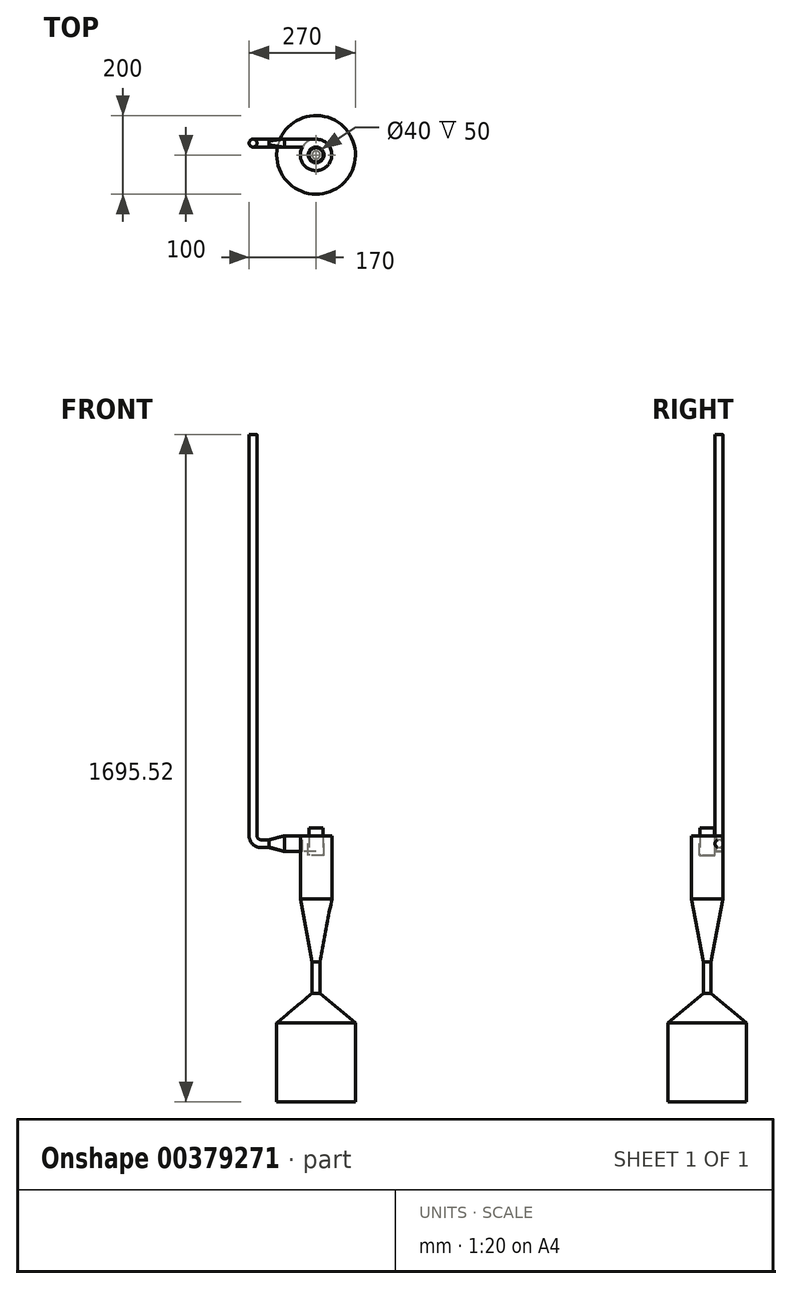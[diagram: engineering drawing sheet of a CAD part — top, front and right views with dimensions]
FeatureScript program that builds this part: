
annotation { "Feature Type Name" : "Feature", "Feature Type Description" : "" }
export const myFeature = defineFeature(function(context is Context, id is Id, definition is map)
    precondition{}
    {
        {
            var Q0;
            Q0=qCreatedBy(makeId("Top.planeOp"),FACE);
            var sketch = newSketch(context, id + "F0", { "sketchPlane" : qUnion([Q0])});
            skCircle(sketch, "E0", {"center": v(0, 0) * mm, "radius": 40 * mm});
            skSolve(sketch);
        }
        {
            var Q0;
            Q0=qSketchRegion(id+"F0",true);
            extrude(context, id + "F1", {"entities" : qUnion([Q0]), "oppositeDirection" : true, "depth" : 160 * mm});
        }
        {
            var Q0;
            Q0=makeQuery(id+"F1.opExtrude","CAP_FACE",FACE,{"disambiguationData":[OSD([sQuery(id+"F0.wireOp",EDGE,"E0")])],"isStart":false});
            cPlane(context, id + "F2", {"entities" : qUnion([Q0]), "cplaneType" : CPlaneType.OFFSET, "offset" : 160 * mm, "width" : 150 * mm, "height" : 150 * mm});
        }
        {
            var Q0;
            Q0=qCreatedBy(id+"F2.planeOp",FACE);
            var sketch = newSketch(context, id + "F3", { "sketchPlane" : qUnion([Q0])});
            skCircle(sketch, "E1", {"center": v(0, 0) * mm, "radius": 10 * mm});
            skSolve(sketch);
        }
        {
            var Q1;
            Q1=makeQuery(id+"F3.imprint","IMPRINT",FACE,{"disambiguationData":[TD([[makeQuery(id+"F3.imprint","IMPRINT",EDGE,{"derivedFrom":sQuery(id+"F3.wireOp",EDGE,"E1")}),1.0]])]});
            var Q2;
            Q2=makeQuery(id+"F1.opExtrude","CAP_FACE",FACE,{"disambiguationData":[OSD([sQuery(id+"F0.wireOp",EDGE,"E0")])],"isStart":false});
            loft(context, id + "F4", {"operationType" : NewBodyOperationType.ADD, "sheetProfilesArray" : [{ "sheetProfileEntities" : qUnion([Q1]) }, { "sheetProfileEntities" : qUnion([Q2]) }]});
        }
        {
            var Q0;
            Q0=makeQuery(id+"F4.opLoft","CAP_FACE",FACE,{"disambiguationData":[OSD([makeQuery(id+"F3.imprint","IMPRINT",FACE,{"disambiguationData":[TD([[makeQuery(id+"F3.imprint","IMPRINT",EDGE,{"derivedFrom":sQuery(id+"F3.wireOp",EDGE,"E1")}),1.0]])]})])],"isStart":true});
            extrude(context, id + "F5", {"entities" : qUnion([Q0]), "operationType" : NewBodyOperationType.ADD, "depth" : 40 * mm});
        }
        {
            var Q0;
            Q0=qCreatedBy(makeId("Top.planeOp"),FACE);
            var sketch = newSketch(context, id + "F6", { "sketchPlane" : qUnion([Q0])});
            skLineSegment(sketch, "E2.bottom", {"start": v(0, 20) * mm, "end": v(-80, 20) * mm});
            skLineSegment(sketch, "E2.top", {"start": v(0, 40) * mm, "end": v(-80, 40) * mm});
            skLineSegment(sketch, "E2.left", {"start": v(0, 20) * mm, "end": v(0, 40) * mm});
            skLineSegment(sketch, "E2.right", {"start": v(-80, 20) * mm, "end": v(-80, 40) * mm});
            skSolve(sketch);
        }
        {
            var Q0;
            Q0=makeQuery(id+"F6.imprint","IMPRINT",FACE,{"disambiguationData":[TD([[makeQuery(id+"F6.imprint","IMPRINT",EDGE,{"derivedFrom":sQuery(id+"F6.wireOp",EDGE,"E2.bottom")}),-1.0]])]});
            extrude(context, id + "F7", {"entities" : qUnion([Q0]), "operationType" : NewBodyOperationType.ADD, "oppositeDirection" : true, "depth" : 40 * mm});
        }
        {
            var Q0;
            Q0=makeQuery(id+"F7.boolean.opBoolean","MERGE",FACE,{"derivedFrom":[makeQuery(id+"F1.opExtrude","CAP_FACE",FACE,{"disambiguationData":[OSD([sQuery(id+"F0.wireOp",EDGE,"E0")])],"isStart":true}),makeQuery(id+"F7.opExtrude","CAP_FACE",FACE,{"disambiguationData":[OSD([sQuery(id+"F6.wireOp",EDGE,"E2.bottom"),sQuery(id+"F6.wireOp",EDGE,"E2.top"),sQuery(id+"F6.wireOp",EDGE,"E2.left"),sQuery(id+"F6.wireOp",EDGE,"E2.right")])],"isStart":true})]});
            var sketch = newSketch(context, id + "F8", { "sketchPlane" : qUnion([Q0])});
            skCircle(sketch, "E3", {"center": v(0, 0) * mm, "radius": 18 * mm});
            skSolve(sketch);
        }
        {
            var Q0;
            Q0=makeQuery(id+"F8.imprint","IMPRINT",FACE,{"disambiguationData":[TD([[makeQuery(id+"F8.imprint","IMPRINT",EDGE,{"derivedFrom":sQuery(id+"F8.wireOp",EDGE,"E3")}),1.0]])]});
            extrude(context, id + "F9", {"entities" : qUnion([Q0]), "operationType" : NewBodyOperationType.ADD, "depth" : 20 * mm});
        }
        {
            var Q0;
            Q0=makeQuery(id+"F7.boolean.opBoolean","MERGE",FACE,{"derivedFrom":[makeQuery(id+"F1.opExtrude","CAP_FACE",FACE,{"disambiguationData":[OSD([sQuery(id+"F0.wireOp",EDGE,"E0")])],"isStart":true}),makeQuery(id+"F7.opExtrude","CAP_FACE",FACE,{"disambiguationData":[OSD([sQuery(id+"F6.wireOp",EDGE,"E2.bottom"),sQuery(id+"F6.wireOp",EDGE,"E2.top"),sQuery(id+"F6.wireOp",EDGE,"E2.left"),sQuery(id+"F6.wireOp",EDGE,"E2.right")])],"isStart":true})]});
            var sketch = newSketch(context, id + "F10", { "sketchPlane" : qUnion([Q0])});
            skCircle(sketch, "E4", {"center": v(0, 0) * mm, "radius": 20 * mm});
            skSolve(sketch);
        }
        {
            var Q0;
            Q0=makeQuery(id+"F10.imprint","IMPRINT",FACE,{"disambiguationData":[TD([[makeQuery(id+"F10.imprint","IMPRINT",EDGE,{"derivedFrom":sQuery(id+"F10.wireOp",EDGE,"E4")}),1.0]])]});
            extrude(context, id + "F11", {"entities" : qUnion([Q0]), "operationType" : NewBodyOperationType.REMOVE, "oppositeDirection" : true, "depth" : 50 * mm});
        }
        {
            var Q0;
            Q0=makeQuery(id+"F7.opExtrude","SWEPT_FACE",FACE,{"disambiguationData":[OSD([sQuery(id+"F6.wireOp",EDGE,"E2.right")])]});
            cPlane(context, id + "F12", {"entities" : qUnion([Q0]), "cplaneType" : CPlaneType.OFFSET, "offset" : 40 * mm, "width" : 150 * mm, "height" : 150 * mm});
        }
        {
            var Q0;
            Q0=qCreatedBy(id+"F12.planeOp",FACE);
            var sketch = newSketch(context, id + "F13", { "sketchPlane" : qUnion([Q0])});
            skPoint(sketch, "E5.middle", {"position": v(-30, -20) * mm});
            skArc(sketch, "E6", {"start": v(-34.47, -11.06) * mm, "mid": v(-40, -20) * mm, "end": v(-34.47, -28.94) * mm});
            skArc(sketch, "E7", {"start": v(-25.53, -11.06) * mm, "mid": v(-30, -10) * mm, "end": v(-34.47, -11.06) * mm});
            skArc(sketch, "E8", {"start": v(-25.53, -28.94) * mm, "mid": v(-20, -20) * mm, "end": v(-25.53, -11.06) * mm});
            skArc(sketch, "E9", {"start": v(-34.47, -28.94) * mm, "mid": v(-30, -30) * mm, "end": v(-25.53, -28.94) * mm});
            skPoint(sketch, "E10.orphan", {"position": v(-20, 0) * mm});
            skPoint(sketch, "E5.top.start.orphan", {"position": v(-20, -40) * mm});
            skPoint(sketch, "E11.orphan", {"position": v(-40, 0) * mm});
            skPoint(sketch, "E12.end.orphan", {"position": v(-40, -40) * mm});
            skSolve(sketch);
        }
        {
            var Q1;
            Q1=makeQuery(id+"F13.imprint","IMPRINT",FACE,{"disambiguationData":[TD([[makeQuery(id+"F13.imprint","IMPRINT",EDGE,{"derivedFrom":sQuery(id+"F13.wireOp",EDGE,"E6")}),1.0]])]});
            var Q2;
            Q2=makeQuery(id+"F7.opExtrude","SWEPT_FACE",FACE,{"disambiguationData":[OSD([sQuery(id+"F6.wireOp",EDGE,"E2.right")])]});
            loft(context, id + "F14", {"operationType" : NewBodyOperationType.ADD, "sheetProfilesArray" : [{ "sheetProfileEntities" : qUnion([Q1]) }, { "sheetProfileEntities" : qUnion([Q2]) }]});
        }
        {
            var Q0;
            Q0=makeQuery(id+"F14.opLoft","CAP_FACE",FACE,{"disambiguationData":[OSD([makeQuery(id+"F13.imprint","IMPRINT",FACE,{"disambiguationData":[TD([[makeQuery(id+"F13.imprint","IMPRINT",EDGE,{"derivedFrom":sQuery(id+"F13.wireOp",EDGE,"E6")}),1.0]])]})])],"isStart":true});
            extrude(context, id + "F15", {"entities" : qUnion([Q0]), "operationType" : NewBodyOperationType.ADD, "depth" : 20 * mm});
        }
        {
            var Q0;
            Q0=qCreatedBy(makeId("Front.planeOp"),FACE);
            cPlane(context, id + "F16", {"entities" : qUnion([Q0]), "cplaneType" : CPlaneType.OFFSET, "offset" : 30 * mm, "oppositeDirection" : true, "width" : 150 * mm, "height" : 150 * mm});
        }
        {
            var Q0;
            Q0=qCreatedBy(id+"F16.planeOp",FACE);
            var sketch = newSketch(context, id + "F17", { "sketchPlane" : qUnion([Q0])});
            skLineSegment(sketch, "E13", {"start": v(0, 0) * mm, "end": v(-140, 0) * mm});
            skLineSegment(sketch, "E14", {"start": v(-140, 0) * mm, "end": v(-140, -20) * mm});
            skArc(sketch, "E15", {"start": v(-140, -20) * mm, "mid": v(-154.14, -14.14) * mm, "end": v(-160, 0) * mm});
            skSolve(sketch);
        }
        {
            var Q0;
            Q0=makeQuery(id+"F15.opExtrude","CAP_FACE",FACE,{"disambiguationData":[OSD([makeQuery(id+"F13.imprint","IMPRINT",FACE,{"disambiguationData":[TD([[makeQuery(id+"F13.imprint","IMPRINT",EDGE,{"derivedFrom":sQuery(id+"F13.wireOp",EDGE,"E6")}),1.0]])]})])],"isStart":false});
            var Q1;
            Q1=sQuery(id+"F17.wireOp",EDGE,"E15");
            sweep(context, id + "F18", {"operationType" : NewBodyOperationType.ADD, "profiles" : qUnion([Q0]), "path" : qUnion([Q1])});
        }
        {
            var Q0;
            Q0=makeQuery(id+"F18.opSweep","CAP_FACE",FACE,{"disambiguationData":[OSD([makeQuery(id+"F13.imprint","IMPRINT",FACE,{"disambiguationData":[TD([[makeQuery(id+"F13.imprint","IMPRINT",EDGE,{"derivedFrom":sQuery(id+"F13.wireOp",EDGE,"E6")}),1.0]])]}),sQuery(id+"F17.wireOp",VERTEX,"E15.end")])],"isStart":false});
            extrude(context, id + "F19", {"entities" : qUnion([Q0]), "operationType" : NewBodyOperationType.ADD, "depth" : 20 * mm});
        }
        {
            var Q0;
            Q0=makeQuery(id+"F19.opExtrude","CAP_FACE",FACE,{"disambiguationData":[OSD([makeQuery(id+"F13.imprint","IMPRINT",FACE,{"disambiguationData":[TD([[makeQuery(id+"F13.imprint","IMPRINT",EDGE,{"derivedFrom":sQuery(id+"F13.wireOp",EDGE,"E6")}),1.0]])]}),sQuery(id+"F17.wireOp",VERTEX,"E15.end")])],"isStart":false});
            extrude(context, id + "F20", {"entities" : qUnion([Q0]), "operationType" : NewBodyOperationType.ADD, "depth" : 1000 * mm});
        }
        {
            var Q0;
            Q0=makeQuery(id+"F5.opExtrude","CAP_FACE",FACE,{"disambiguationData":[OSD([makeQuery(id+"F3.imprint","IMPRINT",FACE,{"disambiguationData":[TD([[makeQuery(id+"F3.imprint","IMPRINT",EDGE,{"derivedFrom":sQuery(id+"F3.wireOp",EDGE,"E1")}),1.0]])]})])],"isStart":false});
            extrude(context, id + "F21", {"entities" : qUnion([Q0]), "operationType" : NewBodyOperationType.ADD, "depth" : 40 * mm});
        }
        {
            var Q0;
            Q0=makeQuery(id+"F21.opExtrude","CAP_FACE",FACE,{"disambiguationData":[OSD([makeQuery(id+"F3.imprint","IMPRINT",FACE,{"disambiguationData":[TD([[makeQuery(id+"F3.imprint","IMPRINT",EDGE,{"derivedFrom":sQuery(id+"F3.wireOp",EDGE,"E1")}),1.0]])]})])],"isStart":false});
            cPlane(context, id + "F22", {"entities" : qUnion([Q0]), "cplaneType" : CPlaneType.OFFSET, "offset" : 75.52 * mm, "width" : 150 * mm, "height" : 150 * mm});
        }
        {
            var Q0;
            Q0=qCreatedBy(id+"F22.planeOp",FACE);
            var sketch = newSketch(context, id + "F23", { "sketchPlane" : qUnion([Q0])});
            skCircle(sketch, "E16", {"center": v(0, 0) * mm, "radius": 100 * mm});
            skSolve(sketch);
        }
        {
            var Q1;
            Q1=makeQuery(id+"F23.imprint","IMPRINT",FACE,{"disambiguationData":[TD([[makeQuery(id+"F23.imprint","IMPRINT",EDGE,{"derivedFrom":sQuery(id+"F23.wireOp",EDGE,"E16")}),1.0]])]});
            var Q2;
            Q2=makeQuery(id+"F21.opExtrude","CAP_FACE",FACE,{"disambiguationData":[OSD([makeQuery(id+"F3.imprint","IMPRINT",FACE,{"disambiguationData":[TD([[makeQuery(id+"F3.imprint","IMPRINT",EDGE,{"derivedFrom":sQuery(id+"F3.wireOp",EDGE,"E1")}),1.0]])]})])],"isStart":false});
            loft(context, id + "F24", {"operationType" : NewBodyOperationType.ADD, "sheetProfilesArray" : [{ "sheetProfileEntities" : qUnion([Q1]) }, { "sheetProfileEntities" : qUnion([Q2]) }]});
        }
        {
            var Q0;
            Q0=makeQuery(id+"F24.opLoft","CAP_FACE",FACE,{"disambiguationData":[OSD([makeQuery(id+"F23.imprint","IMPRINT",FACE,{"disambiguationData":[TD([[makeQuery(id+"F23.imprint","IMPRINT",EDGE,{"derivedFrom":sQuery(id+"F23.wireOp",EDGE,"E16")}),1.0]])]})])],"isStart":true});
            extrude(context, id + "F25", {"entities" : qUnion([Q0]), "operationType" : NewBodyOperationType.ADD, "depth" : 200 * mm});
        }
    });
